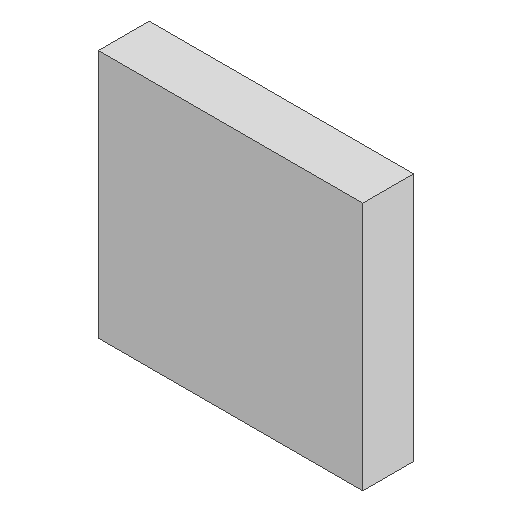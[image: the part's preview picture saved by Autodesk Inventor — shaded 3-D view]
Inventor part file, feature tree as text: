
AUTODESK INVENTOR PART (.ipt)
format: ipt  version: 2025 (Build 290162000, 162)  size: 79,360 bytes
history: native  units: mm
features: extrude x1, sketch x1
ambient origin geometry x8: Origin, YZ Plane, XZ Plane, XY Plane, X Axis, Y Axis, Z Axis, Center Point
bodies: Solid1 (feature_tree)
feature tree (2):
  extrude  "Extrusion1"  Depth=49.0mm
  sketch  "Sketch1"  dims[d0=52.0mm d1=49.0mm d2=10.0mm d3=0.0mm]
